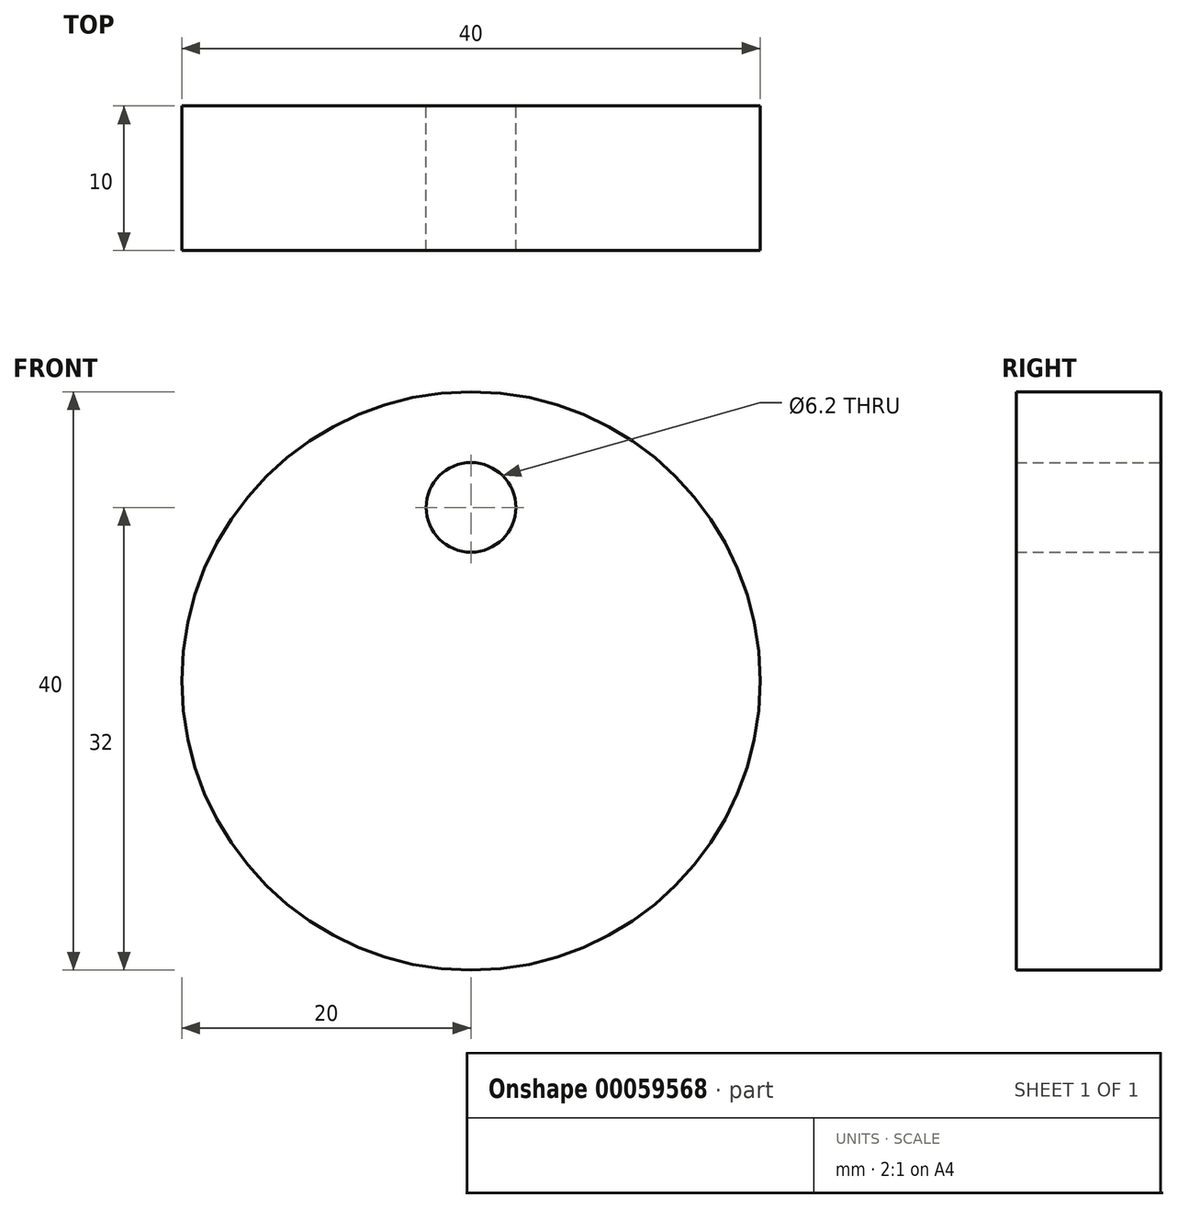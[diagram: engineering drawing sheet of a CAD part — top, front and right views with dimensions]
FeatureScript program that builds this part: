
annotation { "Feature Type Name" : "Feature", "Feature Type Description" : "" }
export const myFeature = defineFeature(function(context is Context, id is Id, definition is map)
    precondition{}
    {
        {
            var Q0;
            Q0=qCreatedBy(makeId("Front.planeOp"),FACE);
            var sketch = newSketch(context, id + "F0", { "sketchPlane" : qUnion([Q0])});
            skCircle(sketch, "E0", {"center": v(0, 0) * mm, "radius": 20 * mm});
            skCircle(sketch, "E1", {"center": v(0, 12) * mm, "radius": 3.1 * mm});
            skSolve(sketch);
        }
        {
            var Q0;
            Q0 = qSketchRegion(id + "F0", true);
            extrude(context, id + "F1", {"entities" : qUnion([Q0]), "depth" : 10 * mm});
        }
    });
